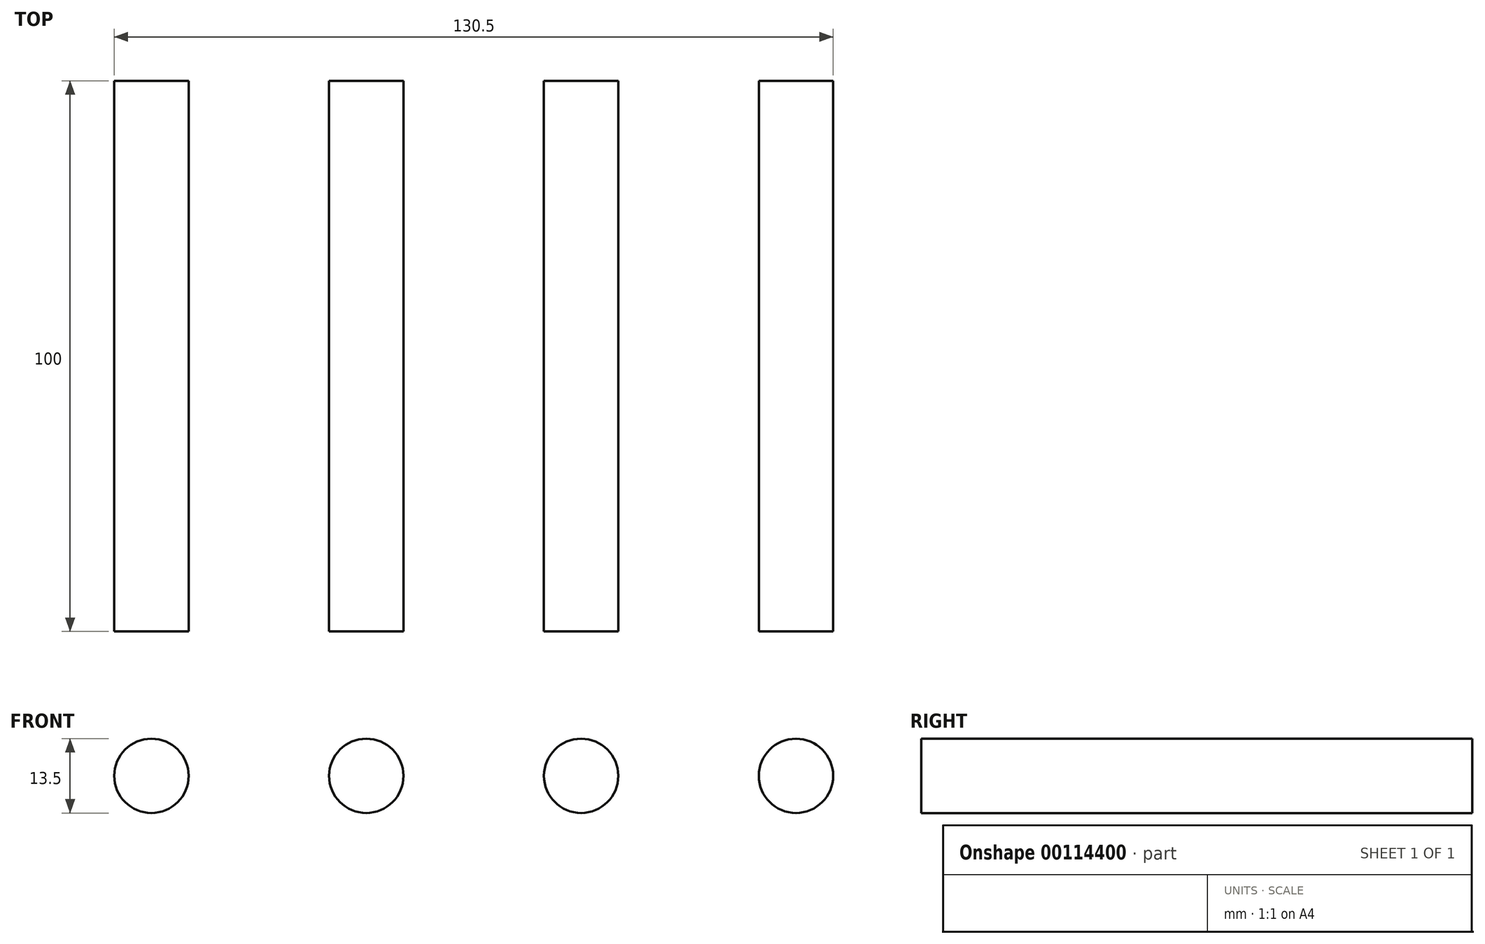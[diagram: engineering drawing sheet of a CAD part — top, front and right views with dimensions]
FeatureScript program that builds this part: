
annotation { "Feature Type Name" : "Feature", "Feature Type Description" : "" }
export const myFeature = defineFeature(function(context is Context, id is Id, definition is map)
    precondition{}
    {
        {
            var Q0;
            Q0=qCreatedBy(makeId("Front.planeOp"),FACE);
            var sketch = newSketch(context, id + "F0", { "sketchPlane" : qUnion([Q0])});
            skCircle(sketch, "E0", {"center": v(0, 0) * mm, "radius": 6.75 * mm});
            skCircle(sketch, "E1", {"center": v(39, 0) * mm, "radius": 6.75 * mm});
            skCircle(sketch, "E2", {"center": v(78, 0) * mm, "radius": 6.75 * mm});
            skCircle(sketch, "E3", {"center": v(-39, 0) * mm, "radius": 6.75 * mm});
            skSolve(sketch);
        }
        {
            var Q0;
            Q0=makeQuery(id+"F0.imprint","IMPRINT",FACE,{"disambiguationData":[TD([[makeQuery(id+"F0.imprint","IMPRINT",EDGE,{"derivedFrom":sQuery(id+"F0.wireOp",EDGE,"E0")}),1.0]])]});
            var Q1;
            Q1=makeQuery(id+"F0.imprint","IMPRINT",FACE,{"disambiguationData":[TD([[makeQuery(id+"F0.imprint","IMPRINT",EDGE,{"derivedFrom":sQuery(id+"F0.wireOp",EDGE,"E1")}),1.0]])]});
            var Q2;
            Q2=makeQuery(id+"F0.imprint","IMPRINT",FACE,{"disambiguationData":[TD([[makeQuery(id+"F0.imprint","IMPRINT",EDGE,{"derivedFrom":sQuery(id+"F0.wireOp",EDGE,"E3")}),1.0]])]});
            var Q3;
            Q3=makeQuery(id+"F0.imprint","IMPRINT",FACE,{"disambiguationData":[TD([[makeQuery(id+"F0.imprint","IMPRINT",EDGE,{"derivedFrom":sQuery(id+"F0.wireOp",EDGE,"E2")}),1.0]])]});
            extrude(context, id + "F1", {"entities" : qUnion([Q0, Q1, Q2, Q3]), "depth" : 50 * mm, "hasSecondDirection" : true, "secondDirectionOppositeDirection" : true, "secondDirectionDepth" : 50 * mm});
        }
    });
